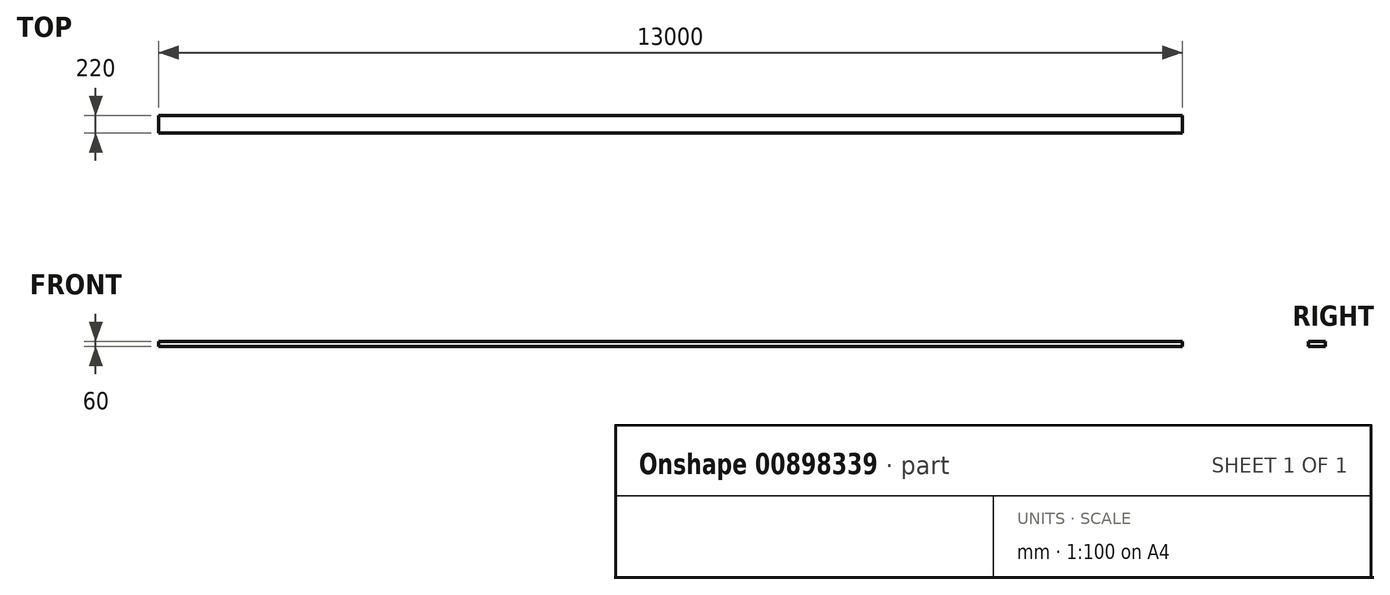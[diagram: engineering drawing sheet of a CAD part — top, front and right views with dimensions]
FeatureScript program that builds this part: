
annotation { "Feature Type Name" : "Feature", "Feature Type Description" : "" }
export const myFeature = defineFeature(function(context is Context, id is Id, definition is map)
    precondition{}
    {
        {
            var Q0;
            Q0=qCreatedBy(makeId("Top.planeOp"),FACE);
            var sketch = newSketch(context, id + "F0", { "sketchPlane" : qUnion([Q0])});
            skLineSegment(sketch, "E0", {"start": v(-6500, 30) * mm, "end": v(-6500, -190) * mm});
            skLineSegment(sketch, "E1", {"start": v(-6500, -190) * mm, "end": v(6500, -190) * mm});
            skLineSegment(sketch, "E2", {"start": v(-6500, 30) * mm, "end": v(6500, 30) * mm});
            skLineSegment(sketch, "E3", {"start": v(6500, 30) * mm, "end": v(6500, -190) * mm});
            skSolve(sketch);
        }
        {
            var Q0;
            Q0=makeQuery(id+"F0.imprint","IMPRINT",FACE,{"disambiguationData":[TD([[makeQuery(id+"F0.imprint","IMPRINT",EDGE,{"derivedFrom":sQuery(id+"F0.wireOp",EDGE,"E0")}),1.0]])]});
            extrude(context, id + "F1", {"entities" : qUnion([Q0]), "depth" : 60 * mm, "offsetDistance" : 25 * mm});
        }
    });
